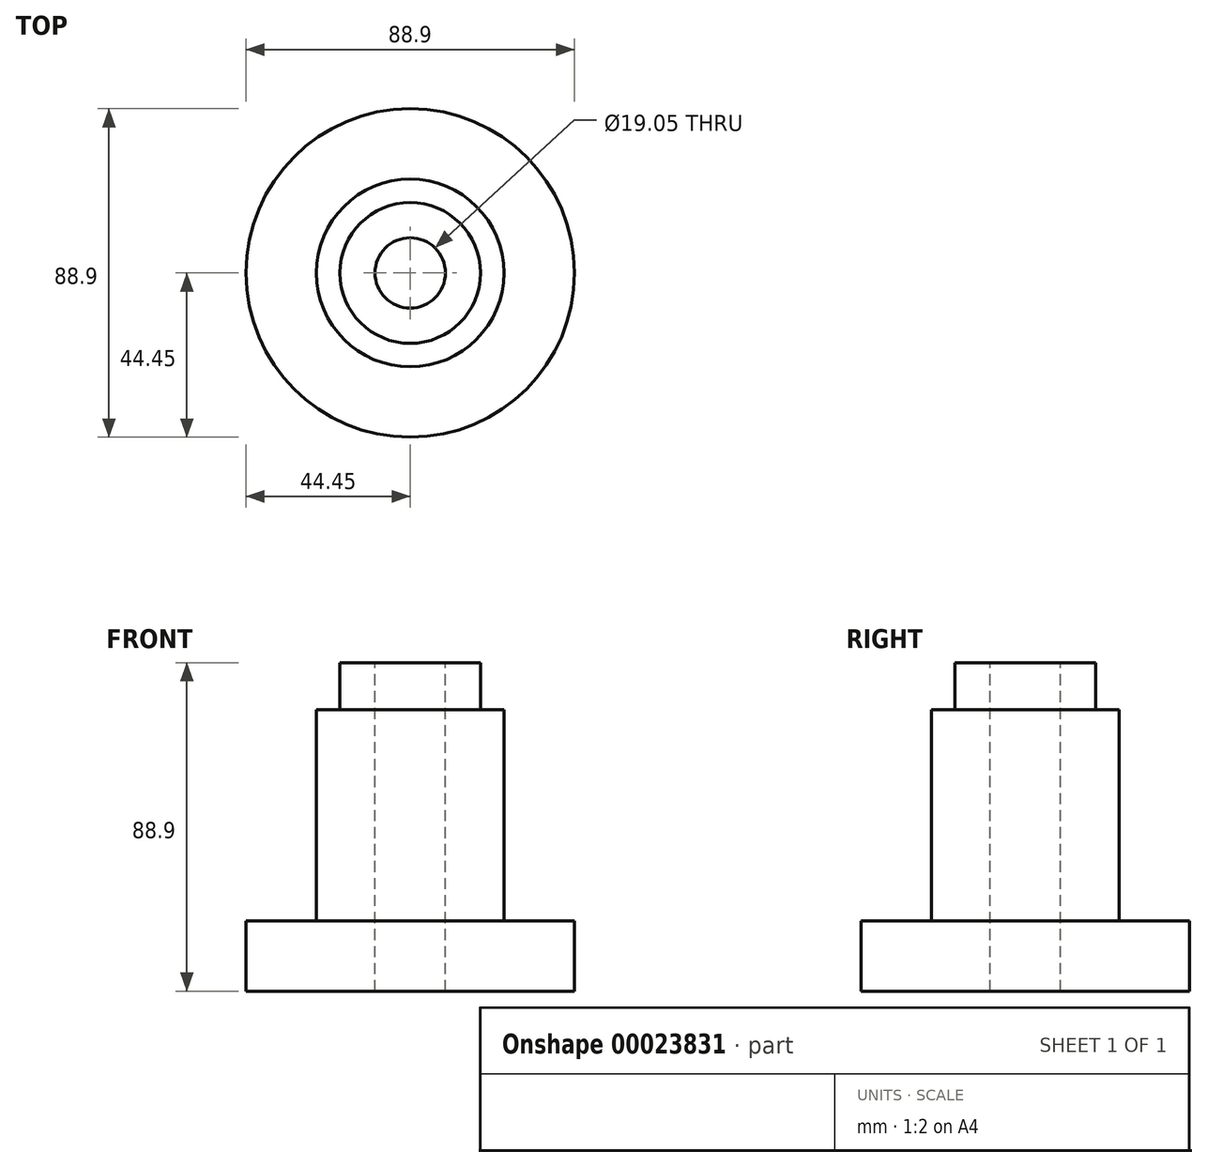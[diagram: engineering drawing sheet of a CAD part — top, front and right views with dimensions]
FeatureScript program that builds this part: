
annotation { "Feature Type Name" : "Feature", "Feature Type Description" : "" }
export const myFeature = defineFeature(function(context is Context, id is Id, definition is map)
    precondition{}
    {
        {
            var Q0;
            Q0=qCreatedBy(makeId("Front.planeOp"),FACE);
            var sketch = newSketch(context, id + "F0", { "sketchPlane" : qUnion([Q0])});
            skLineSegment(sketch, "E0", {"start": v(0, 37.06) * mm, "end": v(0, -37.93) * mm, "construction": true});
            skLineSegment(sketch, "E1.bottom", {"start": v(0, 59.31) * mm, "end": v(-19.05, 59.31) * mm});
            skLineSegment(sketch, "E1.top", {"start": v(0, 46.61) * mm, "end": v(-19.05, 46.61) * mm});
            skLineSegment(sketch, "E1.left", {"start": v(0, 59.31) * mm, "end": v(0, 46.61) * mm});
            skLineSegment(sketch, "E1.right", {"start": v(-19.05, 59.31) * mm, "end": v(-19.05, 46.61) * mm});
            skLineSegment(sketch, "E2.bottom", {"start": v(0, 46.61) * mm, "end": v(-25.4, 46.61) * mm});
            skLineSegment(sketch, "E2.top", {"start": v(0, -10.54) * mm, "end": v(-25.4, -10.54) * mm});
            skLineSegment(sketch, "E2.left", {"start": v(0, 46.61) * mm, "end": v(0, -10.54) * mm});
            skLineSegment(sketch, "E2.right", {"start": v(-25.4, 46.61) * mm, "end": v(-25.4, -10.54) * mm});
            skLineSegment(sketch, "E3.bottom", {"start": v(0, -10.54) * mm, "end": v(-44.45, -10.54) * mm});
            skLineSegment(sketch, "E3.top", {"start": v(0, -29.59) * mm, "end": v(-44.45, -29.59) * mm});
            skLineSegment(sketch, "E3.left", {"start": v(0, -10.54) * mm, "end": v(0, -29.59) * mm});
            skLineSegment(sketch, "E3.right", {"start": v(-44.45, -10.54) * mm, "end": v(-44.45, -29.59) * mm});
            skLineSegment(sketch, "E4", {"start": v(19.05, 79.27) * mm, "end": v(19.05, 76.3) * mm, "construction": true});
            skSolve(sketch);
        }
        {
            var Q0;
            Q0 = qSketchRegion(id + "F0", true);
            var Q1;
            Q1=sQuery(id+"F0.wireOp",EDGE,"E3.left");
            revolve(context, id + "F1", {"entities" : qUnion([Q0]), "axis" : qUnion([Q1]), "revolveType" : RevolveType.FULL});
        }
        {
            var Q0;
            Q0=makeQuery(id+"F1.opRevolve","SWEPT_FACE",FACE,{"disambiguationData":[OSD([sQuery(id+"F0.wireOp",EDGE,"E1.bottom")])]});
            var sketch = newSketch(context, id + "F2", { "sketchPlane" : qUnion([Q0])});
            skCircle(sketch, "E5", {"center": v(0, 0) * mm, "radius": 9.53 * mm});
            skSolve(sketch);
        }
        {
            var Q0;
            Q0 = qSketchRegion(id + "F2", true);
            extrude(context, id + "F3", {"entities" : qUnion([Q0]), "operationType" : NewBodyOperationType.REMOVE, "endBound" : BoundingType.THROUGH_ALL, "oppositeDirection" : true, "depth" : 25.4 * mm});
        }
    });
